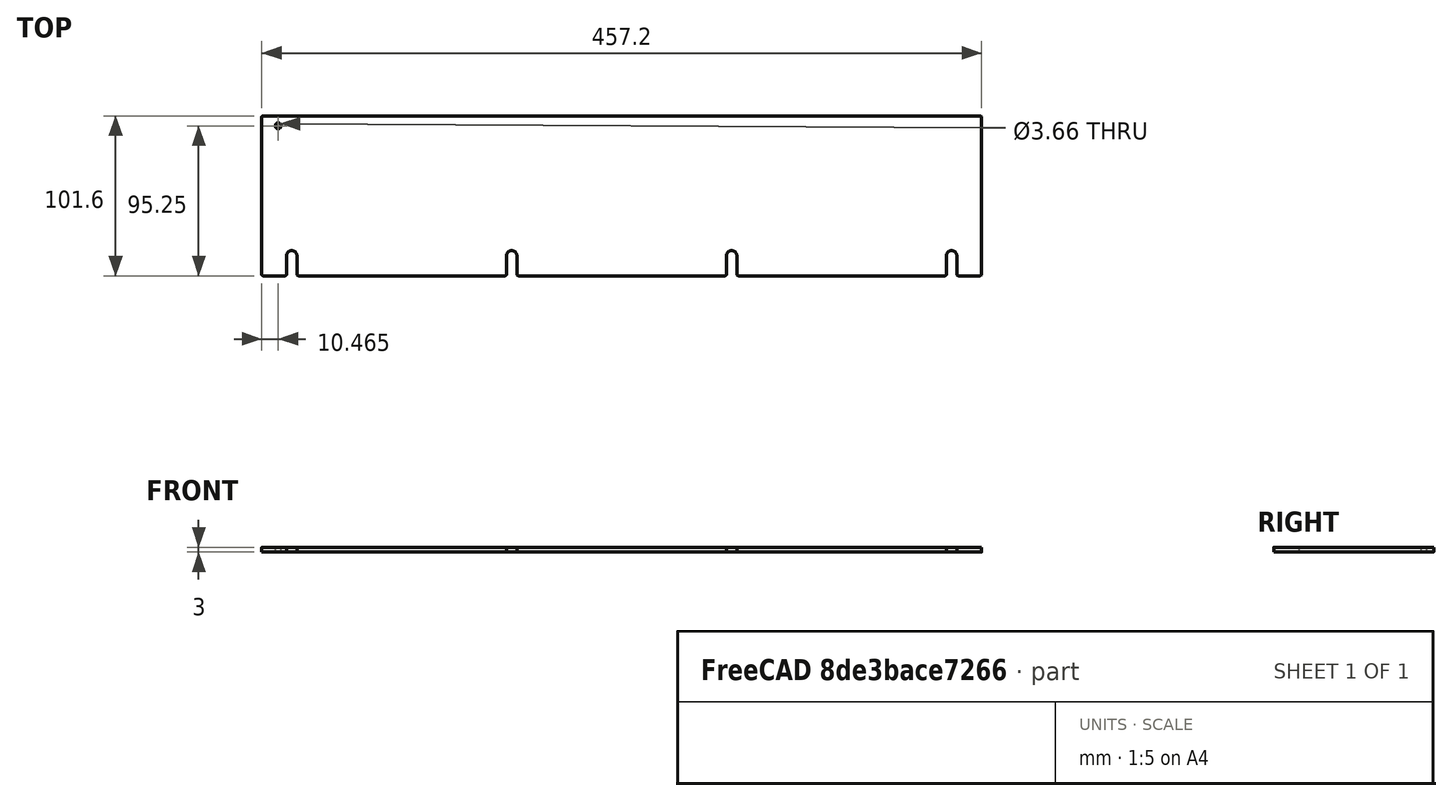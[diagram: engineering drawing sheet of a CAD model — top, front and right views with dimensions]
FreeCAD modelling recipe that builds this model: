
FCSTD DOCUMENT  (FreeCAD 0.21R33675 (Git))
Label: left_wall
License: All rights reserved
LicenseURL: http://en.wikipedia.org/wiki/All_rights_reserved
objects: Sketcher::SketchObject×1, Spreadsheet::Sheet×1, PartDesign::Pad×1, PartDesign::Body×1
note: 4 computed .brp shape members not serialized (recipe doc carries the construction recipe); baked Part::Feature solids carry a one-line shape summary decoded from their .brp

FEATURE [Sketcher::SketchObject] Sketch
  FullyConstrained = true
  MapMode = 5
  Support = -> [XY_Plane]
  expr: Constraints[122] = Spreadsheet.BracketHoleFromSide
  expr: Constraints[125] = Spreadsheet.UpperBracketHoleFromTop
  expr: Constraints[127] = Spreadsheet.BracketHoleDiameter
  expr: Constraints[19] = Spreadsheet.FilletRadius
  expr: Constraints[21] = Spreadsheet.Height
  expr: Constraints[22] = Spreadsheet.Length
  expr: Constraints[27] = Spreadsheet.MountHoleDistanceFromBottom
  expr: Constraints[29] = Spreadsheet.MountHoleDiameter
  expr: Constraints[49] = Spreadsheet.MountHoleSideMargin
  expr: Constraints[53] = Spreadsheet.MountHoleDistanceFromBottom
  sketch-geometry (49):
    g0: ArcOfCircle CenterX=-227.6 CenterY=49.8 CenterZ=0 NormalX=0 NormalY=0 NormalZ=1 AngleXU=0 Radius=1 StartAngle=1.5708 EndAngle=3.14159
    g1: LineSegment StartX=-227.6 StartY=50.8 StartZ=0 EndX=227.6 EndY=50.8 EndZ=0
    g2: ArcOfCircle CenterX=227.6 CenterY=49.8 CenterZ=0 NormalX=0 NormalY=0 NormalZ=1 AngleXU=0 Radius=1 StartAngle=9e-16 EndAngle=1.5708
    g3: LineSegment StartX=228.6 StartY=49.8 StartZ=0 EndX=228.6 EndY=-49.8 EndZ=0
    g4: ArcOfCircle CenterX=227.6 CenterY=-49.8 CenterZ=0 NormalX=0 NormalY=0 NormalZ=1 AngleXU=0 Radius=1 StartAngle=4.71239 EndAngle=6.28319
    g5: LineSegment StartX=227.6 StartY=-50.8 StartZ=0 EndX=-227.6 EndY=-50.8 EndZ=0
    g6: ArcOfCircle CenterX=-227.6 CenterY=-49.8 CenterZ=0 NormalX=0 NormalY=0 NormalZ=1 AngleXU=0 Radius=1 StartAngle=3.14159 EndAngle=4.71239
    g7: LineSegment StartX=-228.6 StartY=-49.8 StartZ=0 EndX=-228.6 EndY=49.8 EndZ=0
    g8: GeomPoint X=-228.6 Y=50.8 Z=0
    g9: GeomPoint X=228.6 Y=-50.8 Z=0
    g10: LineSegment StartX=-69.85 StartY=-38.1 StartZ=0 EndX=69.85 EndY=-38.1 EndZ=0
    g11: LineSegment StartX=0 StartY=-50.8 StartZ=0 EndX=0 EndY=-38.1 EndZ=0
    g12: Circle CenterX=-69.85 CenterY=-38.1 CenterZ=0 NormalX=0 NormalY=0 NormalZ=1 AngleXU=0 Radius=3.302
    g13: Circle CenterX=69.85 CenterY=-38.1 CenterZ=0 NormalX=0 NormalY=0 NormalZ=1 AngleXU=0 Radius=3.302
    g14: LineSegment StartX=-69.85 StartY=-38.1 StartZ=0 EndX=-209.55 EndY=-38.1 EndZ=0
    g15: LineSegment StartX=-209.55 StartY=-38.1 StartZ=0 EndX=-228.6 EndY=-38.1 EndZ=0
    g16: LineSegment StartX=69.85 StartY=-38.1 StartZ=0 EndX=209.55 EndY=-38.1 EndZ=0
    g17: LineSegment StartX=209.55 StartY=-38.1 StartZ=0 EndX=228.6 EndY=-38.1 EndZ=0
    g18: Circle CenterX=-209.55 CenterY=-38.1 CenterZ=0 NormalX=0 NormalY=0 NormalZ=1 AngleXU=0 Radius=3.302
    g19: Circle CenterX=209.55 CenterY=-38.1 CenterZ=0 NormalX=0 NormalY=0 NormalZ=1 AngleXU=0 Radius=3.302
    g20: LineSegment StartX=0 StartY=-38.1 StartZ=0 EndX=0 EndY=-50.8 EndZ=0
    g21: ArcOfCircle CenterX=-209.55 CenterY=-38.1 CenterZ=0 NormalX=0 NormalY=0 NormalZ=1 AngleXU=0 Radius=3.302 StartAngle=8e-16 EndAngle=3.14159
    g22: LineSegment StartX=-212.852 StartY=-38.1 StartZ=0 EndX=-212.852 EndY=-49.8 EndZ=0
    g23: LineSegment StartX=-206.248 StartY=-38.1 StartZ=0 EndX=-206.248 EndY=-49.8 EndZ=0
    g24: ArcOfCircle CenterX=-213.852 CenterY=-49.8 CenterZ=0 NormalX=0 NormalY=0 NormalZ=1 AngleXU=0 Radius=1 StartAngle=4.71239 EndAngle=6.28319
    g25: ArcOfCircle CenterX=-205.248 CenterY=-49.8 CenterZ=0 NormalX=0 NormalY=0 NormalZ=1 AngleXU=0 Radius=1 StartAngle=3.14159 EndAngle=4.71239
    g26: ArcOfCircle CenterX=-69.85 CenterY=-38.1 CenterZ=0 NormalX=0 NormalY=0 NormalZ=1 AngleXU=0 Radius=3.302 StartAngle=5e-16 EndAngle=3.14159
    g27: LineSegment StartX=-73.152 StartY=-38.1 StartZ=0 EndX=-73.152 EndY=-49.8 EndZ=0
    g28: LineSegment StartX=-66.548 StartY=-38.1 StartZ=0 EndX=-66.548 EndY=-49.8 EndZ=0
    g29: ArcOfCircle CenterX=-74.152 CenterY=-49.8 CenterZ=0 NormalX=0 NormalY=0 NormalZ=1 AngleXU=0 Radius=1 StartAngle=4.71239 EndAngle=6.28319
    g30: ArcOfCircle CenterX=-65.548 CenterY=-49.8 CenterZ=0 NormalX=0 NormalY=0 NormalZ=1 AngleXU=0 Radius=1 StartAngle=3.14159 EndAngle=4.71239
    g31: ArcOfCircle CenterX=69.85 CenterY=-38.1 CenterZ=0 NormalX=0 NormalY=0 NormalZ=1 AngleXU=0 Radius=3.302 StartAngle=7e-16 EndAngle=3.14159
    g32: LineSegment StartX=66.548 StartY=-38.1 StartZ=0 EndX=66.548 EndY=-49.8 EndZ=0
    g33: LineSegment StartX=73.152 StartY=-38.1 StartZ=0 EndX=73.152 EndY=-49.8 EndZ=0
    g34: ArcOfCircle CenterX=65.548 CenterY=-49.8 CenterZ=0 NormalX=0 NormalY=0 NormalZ=1 AngleXU=0 Radius=1 StartAngle=4.71239 EndAngle=6.28319
    g35: ArcOfCircle CenterX=74.152 CenterY=-49.8 CenterZ=0 NormalX=0 NormalY=0 NormalZ=1 AngleXU=0 Radius=1 StartAngle=3.14159 EndAngle=4.71239
    g36: ArcOfCircle CenterX=209.55 CenterY=-38.1 CenterZ=0 NormalX=0 NormalY=0 NormalZ=1 AngleXU=0 Radius=3.302 StartAngle=9.1e-15 EndAngle=3.14159
    g37: LineSegment StartX=206.248 StartY=-38.1 StartZ=0 EndX=206.248 EndY=-49.8 EndZ=0
    g38: LineSegment StartX=212.852 StartY=-38.1 StartZ=0 EndX=212.852 EndY=-49.8 EndZ=0
    g39: ArcOfCircle CenterX=205.248 CenterY=-49.8 CenterZ=0 NormalX=0 NormalY=0 NormalZ=1 AngleXU=0 Radius=1 StartAngle=4.71239 EndAngle=6.28319
    g40: ArcOfCircle CenterX=213.852 CenterY=-49.8 CenterZ=0 NormalX=0 NormalY=0 NormalZ=1 AngleXU=0 Radius=1 StartAngle=3.14159 EndAngle=4.71239
    g41: LineSegment StartX=-227.6 StartY=-50.8 StartZ=0 EndX=-213.852 EndY=-50.8 EndZ=0
    g42: LineSegment StartX=-205.248 StartY=-50.8 StartZ=0 EndX=-74.152 EndY=-50.8 EndZ=0
    g43: LineSegment StartX=-65.548 StartY=-50.8 StartZ=0 EndX=65.548 EndY=-50.8 EndZ=0
    g44: LineSegment StartX=74.152 StartY=-50.8 StartZ=0 EndX=205.248 EndY=-50.8 EndZ=0
    g45: LineSegment StartX=213.852 StartY=-50.8 StartZ=0 EndX=227.6 EndY=-50.8 EndZ=0
    g46: LineSegment StartX=-228.6 StartY=50.8 StartZ=0 EndX=-218.135 EndY=50.8 EndZ=0
    g47: LineSegment StartX=-218.135 StartY=50.8 StartZ=0 EndX=-218.135 EndY=44.45 EndZ=0
    g48: Circle CenterX=-218.135 CenterY=44.45 CenterZ=0 NormalX=0 NormalY=0 NormalZ=1 AngleXU=0 Radius=1.8288
  constraints (128):
    c: Tangent(g0,g1) = 1.5708
    c: Tangent(g1,g2) = 1.5708
    c: Tangent(g2,g3) = 1.5708
    c: Tangent(g3,g4) = 1.5708
    c: Tangent(g4,g5) = 1.5708
    c: Tangent(g5,g6) = 1.5708
    c: Tangent(g6,g7) = 1.5708
    c: Tangent(g7,g0) = 1.5708
    c: Horizontal(g1)
    c: Horizontal(g5)
    c: Vertical(g3)
    c: Vertical(g7)
    c: Equal(g0,g2)
    c: Equal(g2,g4)
    c: Equal(g4,g6)
    c: PointOnObject(g8,g1)
    c: PointOnObject(g8,g7)
    c: PointOnObject(g9,g3)
    c: PointOnObject(g9,g5)
    c: Radius(g2) = 1
    c: Symmetric(g8,g9,g-1)
    c: DistanceY(g4,g1) = 101.6
    c: DistanceX(g0,g2) = 457.2
    c: Horizontal(g10)
    c: Vertical(g11)
    c: PointOnObject(g11,g5)
    c: PointOnObject(g11,g-2)
    c: DistanceY(g11,g11) = 12.7
    c: Coincident(g13,g10)
    c: Diameter(g13) = 6.604
    c: Equal(g12,g13)
    c: Coincident(g12,g10)
    c: Coincident(g14,g12)
    c: Horizontal(g14)
    c: Coincident(g15,g14)
    c: PointOnObject(g15,g7)
    c: Horizontal(g15)
    c: Coincident(g16,g13)
    c: Horizontal(g16)
    c: Coincident(g17,g16)
    c: PointOnObject(g17,g3)
    c: Horizontal(g17)
    c: Equal(g17,g15)
    c: Equal(g14,g10)
    c: Equal(g10,g16)
    c: Coincident(g18,g14)
    c: Coincident(g19,g16)
    c: Equal(g18,g12)
    c: Equal(g13,g19)
    c: DistanceX(g15,g15) = 19.05
    c: PointOnObject(g20,g10)
    c: Vertical(g20)
    c: Coincident(g20,g11)
    c: DistanceY(g20,g20) = 12.7
    c: Coincident(g21,g14)
    c: PointOnObject(g21,g15)
    c: PointOnObject(g21,g14)
    c: PointOnObject(g21,g18)
    c: Coincident(g22,g21)
    c: Coincident(g23,g21)
    c: Vertical(g23)
    c: Vertical(g22)
    c: Equal(g22,g23)
    c: Tangent(g24,g22) = 1.5708
    c: Tangent(g24,g5) = 1.5708
    c: Tangent(g25,g23) = -1.5708
    c: Tangent(g25,g5) = 1.5708
    c: Equal(g6,g24)
    c: Coincident(g26,g10)
    c: PointOnObject(g26,g14)
    c: PointOnObject(g26,g10)
    c: PointOnObject(g26,g12)
    c: Coincident(g27,g26)
    c: Vertical(g27)
    c: Coincident(g28,g26)
    c: Vertical(g28)
    c: Equal(g27,g28)
    c: Tangent(g29,g27) = 1.5708
    c: Tangent(g29,g5) = 1.5708
    c: Tangent(g30,g5) = 1.5708
    c: Tangent(g30,g28) = -1.5708
    c: Equal(g29,g25)
    c: Coincident(g31,g10)
    c: PointOnObject(g31,g10)
    c: PointOnObject(g31,g16)
    c: Tangent(g31,g13) = -1.5708
    c: Coincident(g32,g31)
    c: Vertical(g32)
    c: Coincident(g33,g31)
    c: Vertical(g33)
    c: Equal(g32,g33)
    c: Tangent(g34,g32) = 1.5708
    c: Tangent(g34,g5) = 1.5708
    c: Tangent(g35,g33) = -1.5708
    c: Tangent(g35,g5) = 1.5708
    c: Equal(g34,g30)
    c: Coincident(g36,g16)
    c: PointOnObject(g36,g16)
    c: PointOnObject(g36,g17)
    c: Tangent(g36,g19) = -1.5708
    c: Coincident(g37,g36)
    c: Vertical(g37)
    c: Coincident(g38,g36)
    c: Vertical(g38)
    c: Equal(g37,g38)
    c: Tangent(g39,g37) = 1.5708
    c: Tangent(g39,g5) = 1.5708
    c: Tangent(g40,g38) = -1.5708
    c: Tangent(g40,g5) = 1.5708
    c: Equal(g40,g4)
    c: Coincident(g41,g6)
    c: Coincident(g41,g24)
    c: Coincident(g42,g25)
    c: Coincident(g42,g29)
    c: Coincident(g43,g30)
    c: Coincident(g43,g34)
    c: Coincident(g44,g35)
    c: Coincident(g44,g39)
    c: Coincident(g45,g40)
    c: Coincident(g45,g4)
    c: Coincident(g46,g8)
    c: Horizontal(g46)
    c: DistanceX(g46,g46) = 10.4648
    c: Vertical(g47)
    c: Coincident(g47,g46)
    c: DistanceY(g47,g47) = 6.35
    c: Coincident(g48,g47)
    c: Diameter(g48) = 3.6576
FEATURE [Spreadsheet::Sheet] Spreadsheet
  cells = A2='Parameters; A3='Height; B3(Height)==4 in; A4='Length; B4(Length)==18 in; A5='Thickness; B5(Thickness)==3 mm; A6='FilletRadius; B6(FilletRadius)==1 mm; A7='MountHoleDiameter; B7(MountHoleDiameter)==0.26 in; A8='MountHoleDistanceFromBottom; B8(MountHoleDistanceFromBottom)==0.5 in; A9='MountHoleSideMargin; B9(MountHoleSideMargin)==0.75 in; A11='BracketWidth; B11(BracketWidth)==0.5 in; A12='BracketHoleDiameter; B12(BracketHoleDiameter)==0.144 in; A13='BracketHoleOffset; B13(BracketHoleOffset)==0.412 in; A14='UpperBracketHoleFromTop; B14(UpperBracketHoleFromTop)==0.5 * BracketWidth; A15='BracketHoleFromSide; B15(BracketHoleFromSide)==BracketHoleOffset
FEATURE [PartDesign::Pad] Pad
  Direction = (0,0,1)
  Length = 3
  Length2 = 10
  Profile = -> Sketch
  ReferenceAxis = -> Sketch [N_Axis]
  Type = 0
  expr: Length = Spreadsheet.Thickness
FEATURE [PartDesign::Body] Body
  Group = -> [Sketch,Pad]
  Origin = -> Origin
  Tip = -> Pad
